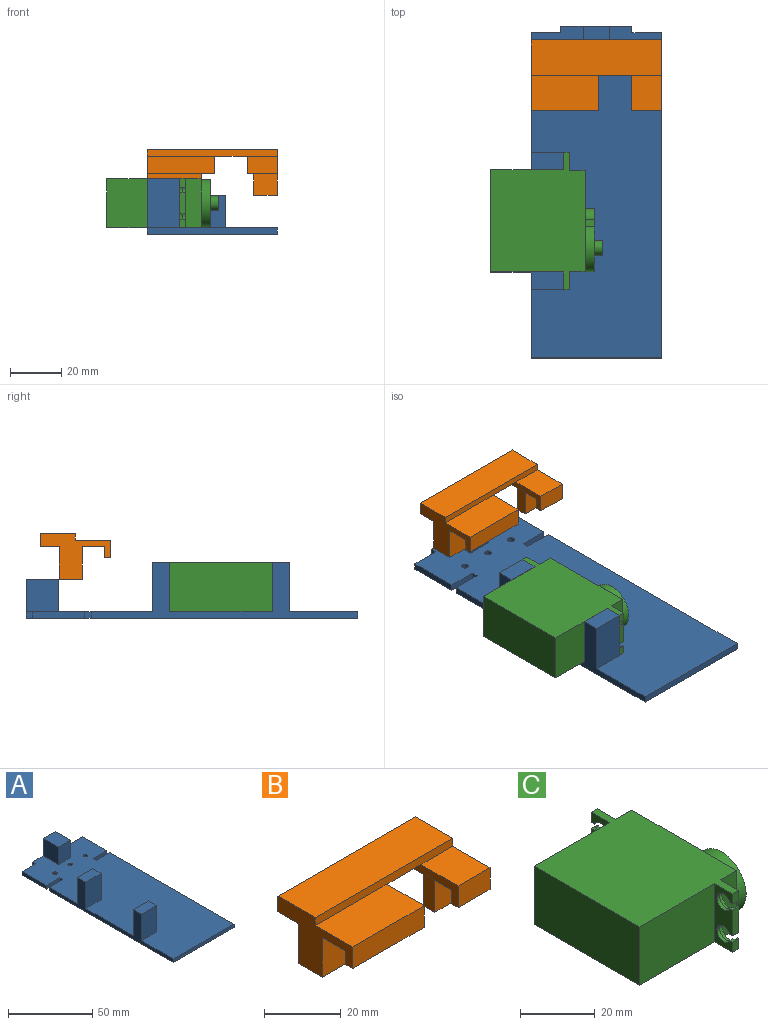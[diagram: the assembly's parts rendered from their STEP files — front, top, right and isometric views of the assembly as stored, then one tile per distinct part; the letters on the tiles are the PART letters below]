
ASSEMBLY  parts=3 mates=1
PART A: 33 faces, bbox 50.8x129.5x21.7 mm
  f0: plane 104.14x21.67mm, normal (-1,0,0), area 526.9mm2, adj f1,f17,f19,f20,f25,f26,f27,f29
  f1: plane 11.43x2.54mm, normal (0,1,0), area 29mm2, adj f0,f2,f19,f20
  f2: plane 2.54x2.54mm, normal (-1,0,0), area 6.5mm2, adj f1,f3,f19,f20
  f3: plane 11.43x2.54mm, normal (0,-1,0), area 29mm2, adj f2,f4,f19,f20
  f4: plane 20.32x2.54mm, normal (-1,0,0), area 51.6mm2, adj f3,f5,f19,f20
  f5: plane 11.43x2.54mm, normal (0,1,0), area 29mm2, adj f4,f6,f19,f20
  f6: plane 2.54x2.54mm, normal (-1,0,0), area 6.5mm2, adj f5,f7,f19,f20
  f7: plane 27.94x15.24mm, normal (0,1,0), area 200mm2, adj f6,f8,f19,f20,f21,f22,f23
  f8: plane 2.54x2.54mm, normal (1,0,0), area 6.5mm2, adj f7,f9,f19,f20
  f9: plane 11.43x2.54mm, normal (0,1,0), area 29mm2, adj f8,f10,f19,f20
  f10: plane 20.32x2.54mm, normal (1,0,0), area 51.6mm2, adj f9,f11,f19,f20
  f11: plane 11.43x2.54mm, normal (0,-1,0), area 29mm2, adj f10,f12,f19,f20
  f12: plane 2.54x2.54mm, normal (1,0,0), area 6.5mm2, adj f11,f13,f19,f20
  f13: plane 11.43x2.54mm, normal (0,1,0), area 29mm2, adj f12,f14,f19,f20
  f14: plane 104.14x2.54mm, normal (1,0,0), area 264.5mm2, adj f13,f17,f19,f20
  f15: cylinder r=1.27mm len=2.54mm, axis (0,0,1), area 20.3mm2, adj f19,f20
  f16: cylinder r=1.27mm len=2.54mm, axis (0,0,1), area 20.3mm2, adj f19,f20
  f17: plane 50.8x2.54mm, normal (0,-1,0), area 129mm2, adj f0,f14,f19,f20
  f18: cylinder r=1.27mm len=2.54mm, axis (0,0,1), area 20.3mm2, adj f19,f20
  f19: plane 129.54x50.8mm, normal (0,0,-1), area 6449.3mm2, adj f0,f1,f2,f3,f4,f5,f6,f7
  f20: plane 129.54x50.8mm, normal (0,0,1), area 6146.1mm2, adj f0,f1,f2,f3,f4,f5,f6,f7
  f21: plane 12.7x10.16mm, normal (0,0,1), area 129mm2, adj f7,f22,f23,f24
  f22: plane 12.7x12.7mm, normal (-1,0,0), area 161.3mm2, adj f7,f20,f21,f24
  f23: plane 12.7x12.7mm, normal (1,0,0), area 161.3mm2, adj f7,f20,f21,f24
  f24: plane 12.7x10.16mm, normal (0,-1,0), area 129mm2, adj f20,f21,f22,f23
  f25: plane 12.7x6.86mm, normal (0,0,1), area 87.1mm2, adj f0,f26,f27,f28
  f26: plane 19.13x12.7mm, normal (0,1,0), area 242.9mm2, adj f0,f20,f25,f28
  f27: plane 19.13x12.7mm, normal (0,-1,0), area 242.9mm2, adj f0,f20,f25,f28
  f28: plane 19.13x6.86mm, normal (1,0,0), area 131.2mm2, adj f20,f25,f26,f27
  f29: plane 12.7x6.86mm, normal (0,0,1), area 87.1mm2, adj f0,f30,f31,f32
  f30: plane 19.13x6.86mm, normal (1,0,0), area 131.2mm2, adj f20,f29,f31,f32
  f31: plane 19.13x12.7mm, normal (0,1,0), area 242.9mm2, adj f0,f20,f29,f30
  f32: plane 19.13x12.7mm, normal (0,-1,0), area 242.9mm2, adj f0,f20,f29,f30
PART B: 35 faces, bbox 50.8x27.5x17.8 mm
  f0: plane 25x11.78mm, normal (0,0,-1), area 210mm2, adj f2,f3,f4,f6,f7,f8,f9,f10
  f1: plane 13.77x11.78mm, normal (0,0,1), area 162.2mm2, adj f2,f13,f15,f32
  f2: plane 27.54x17.78mm, normal (1,0,0), area 223.1mm2, adj f0,f1,f3,f5,f8,f9,f12,f13
  f3: plane 50.8x5.08mm, normal (0,1,0), area 226.2mm2, adj f0,f2,f15,f27,f29,f30,f31,f33
  f4: cylinder r=3.17mm len=6.35mm, axis (0,0,-1), area 50.7mm2, adj f0,f16
  f5: plane 9.22x8.43mm, normal (0,0,-1), area 52.7mm2, adj f2,f6,f7,f8,f9,f10,f11
  f6: plane 12.7x1.4mm, normal (-1,0,0), area 17.8mm2, adj f0,f5,f7,f10
  f7: cylinder r=4.45mm len=12.7mm, axis (0,0,1), area 66.1mm2, adj f0,f5,f6,f8
  f8: plane 12.7x0.99mm, normal (0,1,0), area 12.5mm2, adj f0,f2,f5,f7
  f9: plane 12.7x9.22mm, normal (0,-1,0), area 117.2mm2, adj f0,f2,f5,f11
  f10: plane 12.7x4.14mm, normal (0,1,0), area 52.6mm2, adj f0,f5,f6,f11
  f11: plane 12.7x4.31mm, normal (-1,0,0), area 54.8mm2, adj f0,f5,f9,f10
  f12: plane 11.78x2.54mm, normal (0,0,-1), area 29.9mm2, adj f2,f13,f14,f15
  f13: plane 11.78x6.89mm, normal (0,-1,0), area 81.2mm2, adj f1,f2,f12,f15
  f14: plane 11.78x4.35mm, normal (0,1,0), area 51.3mm2, adj f0,f2,f12,f15
  f15: plane 27.54x6.89mm, normal (-1,0,0), area 81mm2, adj f0,f1,f3,f12,f13,f14,f33
  f16: plane 6.35x6.35mm, normal (0,0,-1), area 31.7mm2, adj f4
  f17: plane 21.28x8.88mm, normal (0,0,-1), area 169.1mm2, adj f19,f20,f21,f22,f23,f27
  f18: plane 26.46x2.54mm, normal (0,0,-1), area 67.2mm2, adj f24,f26,f27,f30
  f19: plane 12.7x0.82mm, normal (0,1,0), area 10.5mm2, adj f17,f20,f27,f29
  f20: cylinder r=4.45mm len=12.7mm, axis (0,0,1), area 144.3mm2, adj f17,f19,f21,f29
  f21: plane 12.7x11.94mm, normal (0,1,0), area 151.7mm2, adj f17,f20,f22,f29
  f22: plane 12.7x8.88mm, normal (1,0,0), area 112.8mm2, adj f17,f21,f23,f29
  f23: plane 21.28x12.7mm, normal (0,-1,0), area 270.2mm2, adj f17,f22,f27,f29
  f24: plane 26.46x4.35mm, normal (0,1,0), area 115.2mm2, adj f18,f27,f29,f30
  f25: cylinder r=3.17mm len=6.35mm, axis (0,0,-1), area 50.7mm2, adj f29,f34
  f26: plane 26.46x6.89mm, normal (0,-1,0), area 182.4mm2, adj f18,f27,f28,f30
  f27: plane 27.54x17.78mm, normal (-1,0,0), area 228.8mm2, adj f3,f17,f18,f19,f23,f24,f26,f28
  f28: plane 26.46x13.77mm, normal (0,0,1), area 364.4mm2, adj f26,f27,f30,f32
  f29: plane 26.46x25mm, normal (0,0,-1), area 460.7mm2, adj f3,f19,f20,f21,f22,f23,f24,f25
  f30: plane 27.54x6.89mm, normal (1,0,0), area 81mm2, adj f3,f18,f24,f26,f28,f29,f33
  f31: plane 50.8x13.77mm, normal (0,0,1), area 699.5mm2, adj f2,f3,f27,f32
  f32: plane 50.8x2.54mm, normal (0,-1,0), area 129mm2, adj f1,f2,f27,f28,f31,f33
  f33: plane 13.77x12.56mm, normal (0,0,-1), area 173mm2, adj f3,f15,f30,f32
  f34: plane 6.35x6.35mm, normal (0,0,-1), area 31.7mm2, adj f25
PART C: 45 faces, bbox 43.7x53.6x19.1 mm
  f0: plane 19.05x6.99mm, normal (1,0,0), area 72.7mm2, adj f1,f2,f6,f8,f12,f14,f17,f19
  f1: plane 3.3x2.29mm, normal (0,1,0), area 7.5mm2, adj f0,f5,f14,f37
  f2: plane 8.38x2.29mm, normal (0,1,0), area 19.2mm2, adj f0,f5,f34,f35
  f3: plane 8.38x2.29mm, normal (0,-1,0), area 19.2mm2, adj f10,f16,f27,f31
  f4: plane 3.3x2.29mm, normal (0,-1,0), area 7.5mm2, adj f10,f14,f16,f28
  f5: plane 19.05x6.86mm, normal (-1,0,0), area 86mm2, adj f1,f2,f11,f12,f14,f17,f32,f33
  f6: cylinder r=3.05mm len=6.1mm, axis (1,0,0), area 21.7mm2, adj f0,f7,f35,f37
  f7: plane 6.1x5.92mm, normal (1,0,0), area 7.9mm2, adj f6,f35,f36,f37
  f8: cylinder r=3.05mm len=6.1mm, axis (1,0,0), area 21.7mm2, adj f0,f9,f32,f34
  f9: plane 6.1x5.92mm, normal (1,0,0), area 7.9mm2, adj f8,f32,f33,f34
  f10: plane 19.05x6.99mm, normal (1,0,0), area 72.7mm2, adj f3,f4,f12,f14,f18,f20,f22,f24
  f11: plane 28.45x19.05mm, normal (0,1,0), area 541.9mm2, adj f5,f12,f14,f15
  f12: plane 53.59x36.83mm, normal (0,0,1), area 1498.5mm2, adj f0,f5,f10,f11,f13,f15,f16,f17
  f13: plane 28.45x19.05mm, normal (0,-1,0), area 541.9mm2, adj f12,f14,f15,f16
  f14: plane 53.59x36.83mm, normal (0,0,-1), area 1498.5mm2, adj f0,f1,f4,f5,f10,f11,f13,f15
  f15: plane 39.88x19.05mm, normal (-1,0,0), area 759.7mm2, adj f11,f12,f13,f14
  f16: plane 19.05x6.86mm, normal (-1,0,0), area 86mm2, adj f3,f4,f12,f13,f14,f18,f26,f27
  f17: plane 3.3x2.29mm, normal (0,1,0), area 7.5mm2, adj f0,f5,f12,f32
  f18: plane 3.3x2.29mm, normal (0,-1,0), area 7.5mm2, adj f10,f12,f16,f30
  f19: plane 19.05x6.1mm, normal (0,1,0), area 116.1mm2, adj f0,f12,f14,f21
  f20: plane 19.05x6.1mm, normal (0,-1,0), area 116.1mm2, adj f10,f12,f14,f21
  f21: plane 39.62x19.05mm, normal (1,0,0), area 437.2mm2, adj f12,f14,f19,f20,f38,f39,f40,f41
  f22: cylinder r=3.05mm len=6.1mm, axis (1,0,0), area 21.7mm2, adj f10,f23,f30,f31
  f23: plane 6.1x5.92mm, normal (1,0,0), area 7.9mm2, adj f22,f29,f30,f31
  f24: cylinder r=3.05mm len=6.1mm, axis (1,0,0), area 21.7mm2, adj f10,f25,f27,f28
  f25: plane 6.1x5.92mm, normal (1,0,0), area 7.9mm2, adj f24,f26,f27,f28
  f26: cylinder r=2.54mm len=5.08mm, axis (1,0,0), area 14.1mm2, adj f16,f25,f27,f28
  f27: plane 2.29x1.16mm, normal (0,0,-1), area 2mm2, adj f3,f10,f16,f24,f25,f26
  f28: plane 2.29x1.16mm, normal (0,0,1), area 2mm2, adj f4,f10,f16,f24,f25,f26
  f29: cylinder r=2.54mm len=5.08mm, axis (1,0,0), area 14.1mm2, adj f16,f23,f30,f31
  f30: plane 2.29x1.16mm, normal (0,0,-1), area 2mm2, adj f10,f16,f18,f22,f23,f29
  f31: plane 2.29x1.16mm, normal (0,0,1), area 2mm2, adj f3,f10,f16,f22,f23,f29
  f32: plane 2.29x1.16mm, normal (0,0,-1), area 2mm2, adj f0,f5,f8,f9,f17,f33
  f33: cylinder r=2.54mm len=5.08mm, axis (1,0,0), area 14.1mm2, adj f5,f9,f32,f34
  f34: plane 2.29x1.16mm, normal (0,0,1), area 2mm2, adj f0,f2,f5,f8,f9,f33
  f35: plane 2.29x1.16mm, normal (0,0,-1), area 2mm2, adj f0,f2,f5,f6,f7,f36
  f36: cylinder r=2.54mm len=5.08mm, axis (1,0,0), area 14.1mm2, adj f5,f7,f35,f37
  f37: plane 2.29x1.16mm, normal (0,0,1), area 2mm2, adj f0,f1,f5,f6,f7,f36
  f38: plane 3.56x2.85mm, normal (0,0,1), area 10.1mm2, adj f21,f39,f41,f42
  f39: cylinder r=9.27mm len=18.54mm, axis (-1,0,0), area 175.2mm2, adj f21,f38,f40,f42
  f40: plane 3.56x2.85mm, normal (0,0,-1), area 10.1mm2, adj f21,f39,f41,f42
  f41: cylinder r=4.32mm len=8.64mm, axis (-1,0,0), area 48.2mm2, adj f21,f38,f40,f42
  f42: plane 24.64x18.54mm, normal (1,0,0), area 293.1mm2, adj f38,f39,f40,f41,f43
  f43: cylinder r=2.79mm len=5.59mm, axis (-1,0,0), area 58mm2, adj f42,f44
  f44: plane 5.59x5.59mm, normal (1,0,0), area 24.5mm2, adj f43
PLACE A t=(-138.03,-10.38,24.77)mm
PLACE B t=(-138.03,-10.38,24.77)mm
PLACE C t=(-138.03,-10.38,24.77)mm
MATE fastened A.f25 <-> C.f12  axis (0,0,1) through (-150.73,-106.39,31.2)mm
